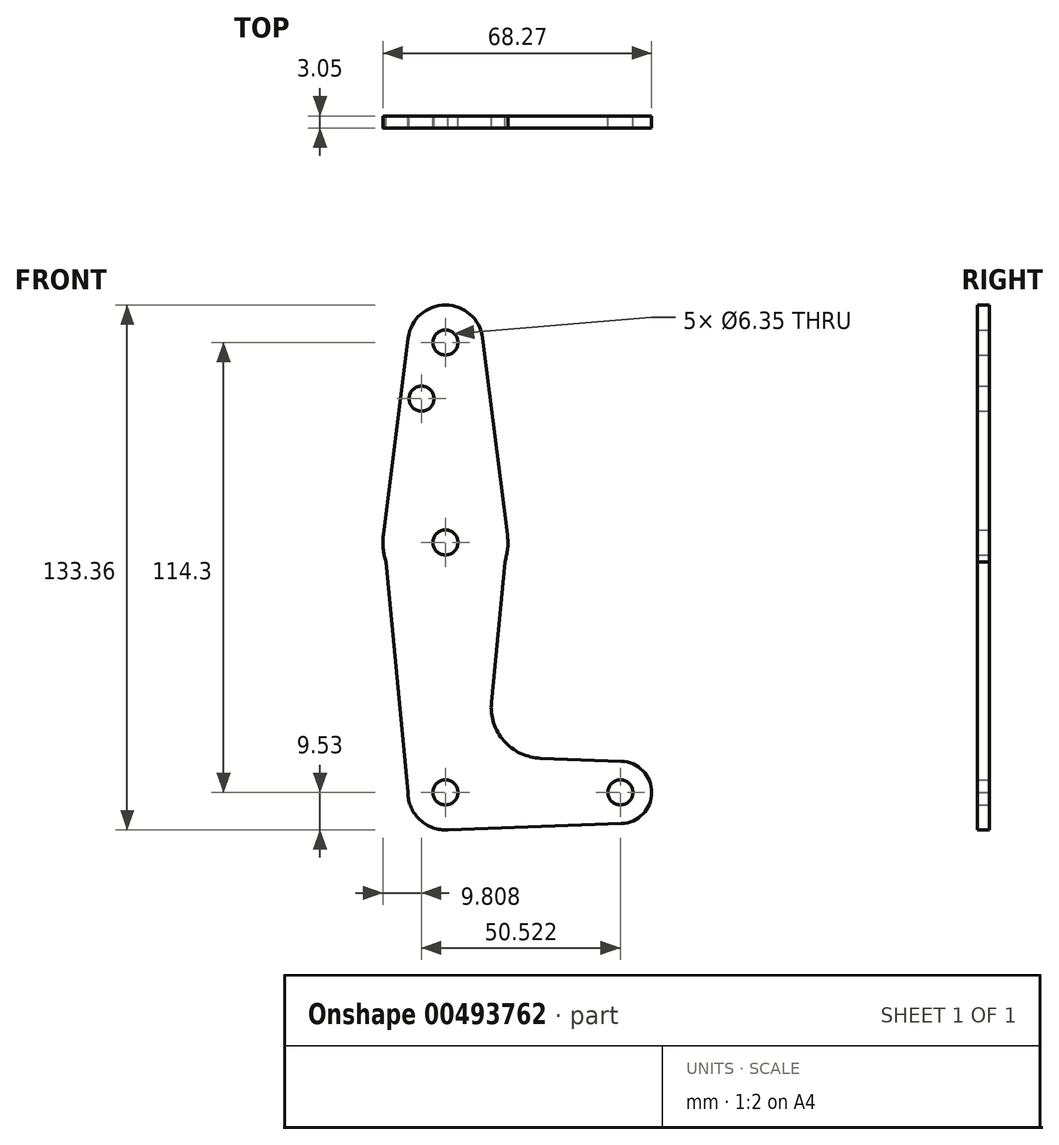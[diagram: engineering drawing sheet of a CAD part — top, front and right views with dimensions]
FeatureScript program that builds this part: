
annotation { "Feature Type Name" : "Feature", "Feature Type Description" : "" }
export const myFeature = defineFeature(function(context is Context, id is Id, definition is map)
    precondition{}
    {
        {
            var Q0;
            Q0=qCreatedBy(makeId("Front.planeOp"),FACE);
            var sketch = newSketch(context, id + "F0", { "sketchPlane" : qUnion([Q0])});
            skLineSegment(sketch, "E0", {"start": v(0, 0) * mm, "end": v(0, 114.3) * mm, "construction": true});
            skLineSegment(sketch, "E1", {"start": v(0, 0) * mm, "end": v(44.45, 0) * mm, "construction": true});
            skCircle(sketch, "E2", {"center": v(0, 114.3) * mm, "radius": 9.53 * mm});
            skCircle(sketch, "E3", {"center": v(0, 63.5) * mm, "radius": 15.88 * mm});
            skCircle(sketch, "E4", {"center": v(0, 0) * mm, "radius": 9.53 * mm});
            skCircle(sketch, "E5", {"center": v(44.45, 0) * mm, "radius": 7.94 * mm});
            skLineSegment(sketch, "E6", {"start": v(-9.45, 115.5) * mm, "end": v(-15.75, 65.48) * mm});
            skLineSegment(sketch, "E7", {"start": v(9.45, 115.5) * mm, "end": v(15.75, 65.48) * mm});
            skLineSegment(sketch, "E8", {"start": v(24.2, 8.66) * mm, "end": v(44.73, 7.93) * mm});
            skLineSegment(sketch, "E9", {"start": v(0, -9.53) * mm, "end": v(44.73, -7.93) * mm});
            skLineSegment(sketch, "E10", {"start": v(-9.52, 0) * mm, "end": v(-15.75, 65.48) * mm});
            skLineSegment(sketch, "E11", {"start": v(11.7, 22.9) * mm, "end": v(15.75, 65.48) * mm});
            skCircle(sketch, "E12", {"center": v(-6.07, 100.03) * mm, "radius": 3.18 * mm});
            skCircle(sketch, "E13", {"center": v(0, 114.3) * mm, "radius": 3.18 * mm});
            skCircle(sketch, "E14", {"center": v(0, 63.5) * mm, "radius": 3.18 * mm});
            skCircle(sketch, "E15", {"center": v(0, 0) * mm, "radius": 3.18 * mm});
            skCircle(sketch, "E16", {"center": v(44.45, 0) * mm, "radius": 3.18 * mm});
            skPoint(sketch, "E17.newPointA", {"position": v(9.52, 0) * mm});
            skArc(sketch, "E17.filletArc", {"start": v(11.7, 22.9) * mm, "mid": v(14.88, 13.09) * mm, "end": v(24.2, 8.66) * mm});
            skSolve(sketch);
        }
        {
            var Q0;
            Q0 = qSketchRegion(id + "F0", true);
            extrude(context, id + "F1", {"entities" : qUnion([Q0]), "depth" : 3.05 * mm});
        }
    });
